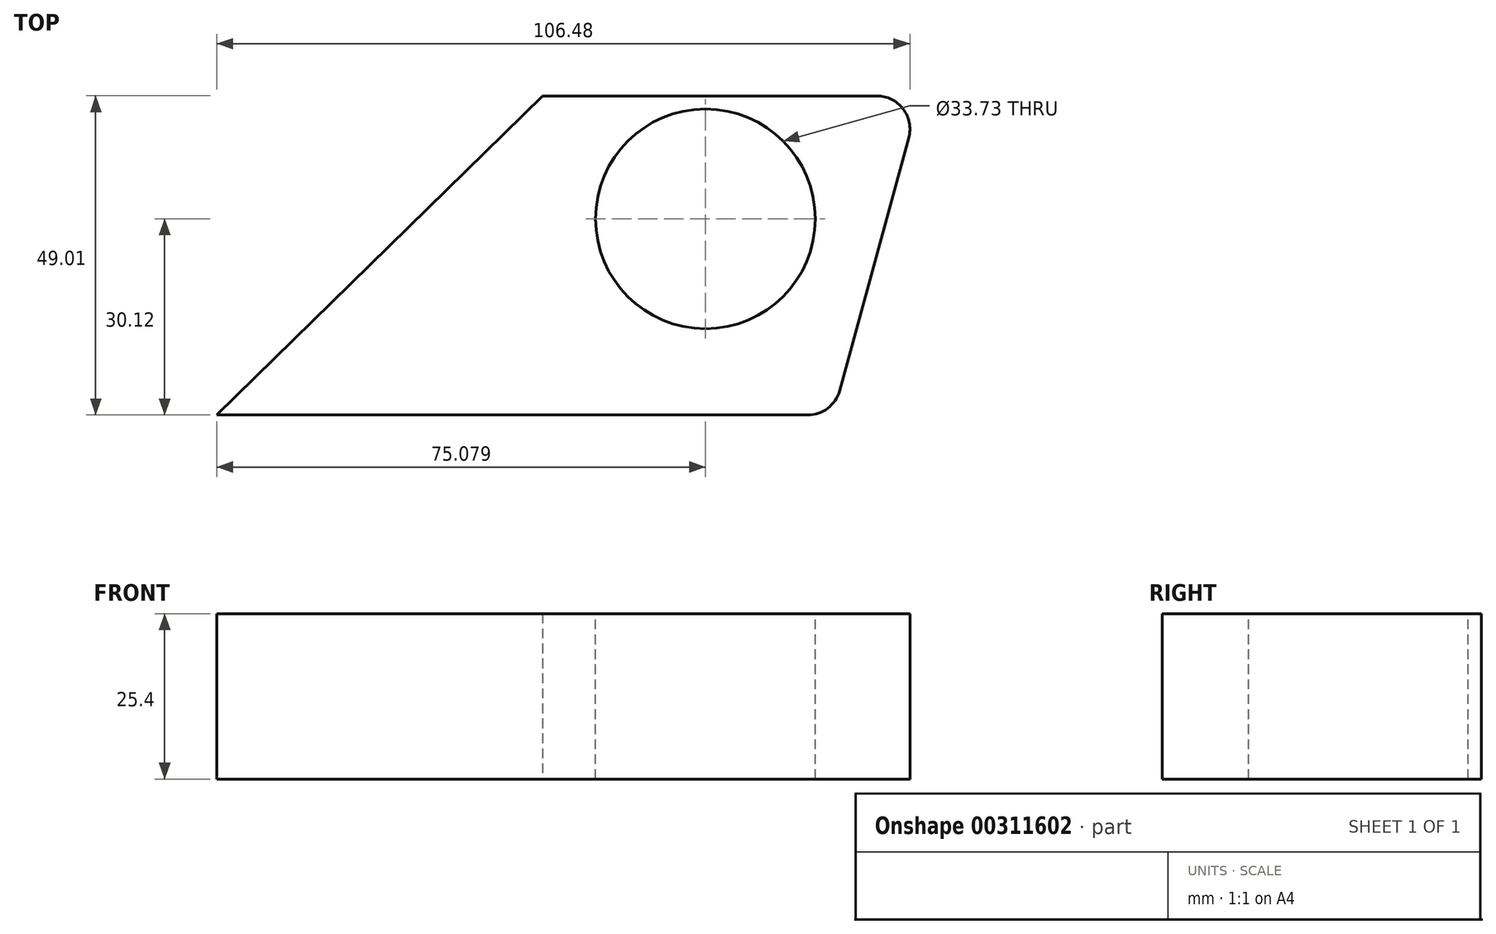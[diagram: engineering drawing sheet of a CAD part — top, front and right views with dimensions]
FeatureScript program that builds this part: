
annotation { "Feature Type Name" : "Feature", "Feature Type Description" : "" }
export const myFeature = defineFeature(function(context is Context, id is Id, definition is map)
    precondition{}
    {
        {
            var Q0;
            Q0=qCreatedBy(makeId("Top.planeOp"),FACE);
            var sketch = newSketch(context, id + "F0", { "sketchPlane" : qUnion([Q0])});
            skLineSegment(sketch, "E0", {"start": v(0, 61.34) * mm, "end": v(57.99, 61.34) * mm});
            skLineSegment(sketch, "E1", {"start": v(57.99, 61.34) * mm, "end": v(44.6, 12.33) * mm});
            skLineSegment(sketch, "E2", {"start": v(44.6, 12.33) * mm, "end": v(-50.07, 12.33) * mm});
            skLineSegment(sketch, "E3", {"start": v(-50.07, 12.33) * mm, "end": v(0, 61.34) * mm});
            skSolve(sketch);
        }
        {
            var Q0;
            Q0 = qSketchRegion(id + "F0", true);
            extrude(context, id + "F1", {"entities" : qUnion([Q0]), "depth" : 25.4 * mm});
        }
        {
            var Q0;
            Q0=makeQuery(id+"F1.opExtrude","CAP_FACE",FACE,{"disambiguationData":[OSD([sQuery(id+"F0.wireOp",EDGE,"E0"),sQuery(id+"F0.wireOp",EDGE,"E1"),sQuery(id+"F0.wireOp",EDGE,"E2"),sQuery(id+"F0.wireOp",EDGE,"E3")])],"isStart":false});
            var sketch = newSketch(context, id + "F2", { "sketchPlane" : qUnion([Q0])});
            skCircle(sketch, "E4", {"center": v(25, 42.45) * mm, "radius": 16.87 * mm});
            skSolve(sketch);
        }
        {
            var Q0;
            Q0=makeQuery(id+"F2.imprint","IMPRINT",FACE,{"disambiguationData":[TD([[makeQuery(id+"F2.imprint","IMPRINT",EDGE,{"derivedFrom":sQuery(id+"F2.wireOp",EDGE,"E4")}),1.0]])]});
            extrude(context, id + "F3", {"entities" : qUnion([Q0]), "operationType" : NewBodyOperationType.REMOVE, "oppositeDirection" : true, "depth" : 25.4 * mm});
        }
        {
            var Q0;
            Q0=makeQuery(id+"F1.opExtrude","SWEPT_EDGE",EDGE,{"disambiguationData":[OSD([sQuery(id+"F0.wireOp",EDGE,"E1"),sQuery(id+"F0.wireOp",EDGE,"E2")])]});
            var Q1;
            Q1=makeQuery(id+"F1.opExtrude","SWEPT_EDGE",EDGE,{"disambiguationData":[OSD([sQuery(id+"F0.wireOp",EDGE,"E0"),sQuery(id+"F0.wireOp",EDGE,"E1")])]});
            fillet(context, id + "F4", {"entities" : qUnion([Q0, Q1]), "radius" : 5.08 * mm, "tangentPropagation" : true, "allowEdgeOverflow" : false});
        }
    });
